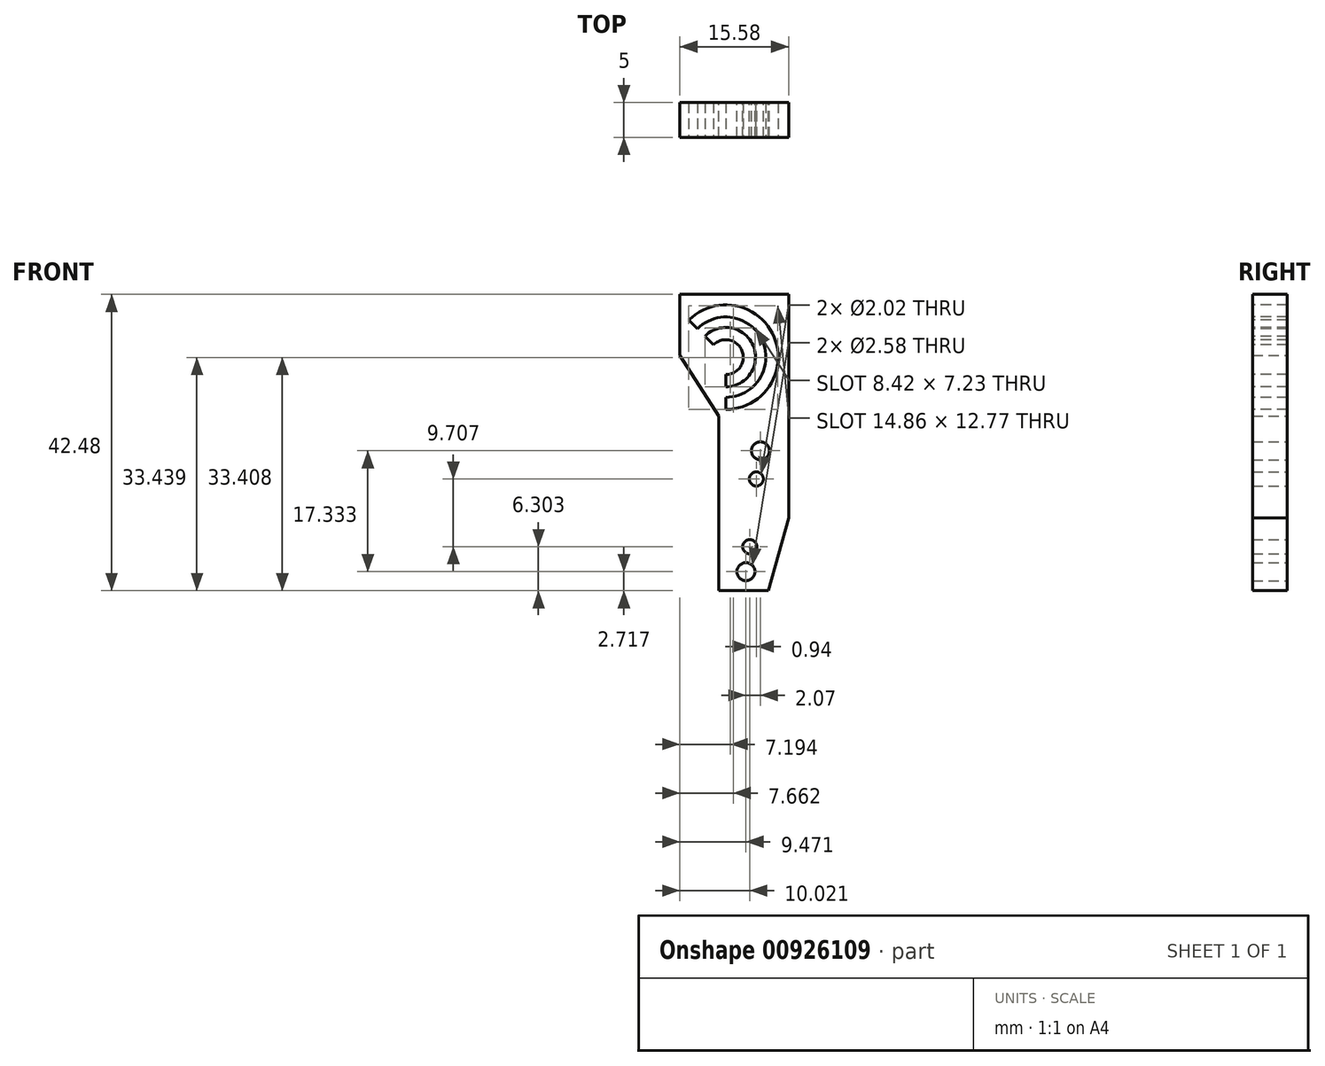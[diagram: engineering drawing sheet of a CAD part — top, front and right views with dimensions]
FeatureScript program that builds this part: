
annotation { "Feature Type Name" : "Feature", "Feature Type Description" : "" }
export const myFeature = defineFeature(function(context is Context, id is Id, definition is map)
    precondition{}
    {
        {
            var Q0;
            Q0=qCreatedBy(makeId("Front.planeOp"),FACE);
            var sketch = newSketch(context, id + "F0", { "sketchPlane" : qUnion([Q0])});
            skLineSegment(sketch, "E0", {"start": v(-37.2, 26.47) * mm, "end": v(-21.63, 26.47) * mm});
            skLineSegment(sketch, "E1", {"start": v(-31.6, -16.01) * mm, "end": v(-24.5, -16.01) * mm});
            skLineSegment(sketch, "E2", {"start": v(-21.63, 26.47) * mm, "end": v(-21.63, -5.57) * mm});
            skLineSegment(sketch, "E3", {"start": v(-21.63, -5.57) * mm, "end": v(-24.5, -16.01) * mm});
            skCircle(sketch, "E4", {"center": v(-27.74, -13.3) * mm, "radius": 1.29 * mm});
            skCircle(sketch, "E5", {"center": v(-27.19, -9.7) * mm, "radius": 1.01 * mm});
            skLineSegment(sketch, "E6", {"start": v(-31.6, 9.02) * mm, "end": v(-31.6, -16.01) * mm});
            skCircle(sketch, "E7", {"center": v(-26.25, 0) * mm, "radius": 1.01 * mm});
            skCircle(sketch, "E8", {"center": v(-25.67, 4.04) * mm, "radius": 1.29 * mm});
            skLineSegment(sketch, "E9", {"start": v(-37.2, 26.47) * mm, "end": v(-37.2, 17.75) * mm});
            skLineSegment(sketch, "E10", {"start": v(-31.6, 9.02) * mm, "end": v(-37.2, 17.75) * mm});
            skSolve(sketch);
        }
        {
            var Q0;
            Q0=qSketchRegion(id+"F0",true);
            extrude(context, id + "F1", {"entities" : qUnion([Q0]), "depth" : 5 * mm, "offsetDistance" : 25 * mm});
        }
        {
            var Q0;
            Q0=makeQuery(id+"F1.opExtrude","CAP_FACE",FACE,{"disambiguationData":[OSD([sQuery(id+"F0.wireOp",EDGE,"E0"),sQuery(id+"F0.wireOp",EDGE,"vhafAufr-sMwy-97n5-iXBO-xDqB0n5jxu3E"),sQuery(id+"F0.wireOp",EDGE,"UXBwDhYX-UGdj-3Fuf-0lg6-L2S2GxCH4KdO"),sQuery(id+"F0.wireOp",EDGE,"E1"),sQuery(id+"F0.wireOp",EDGE,"E2"),sQuery(id+"F0.wireOp",EDGE,"E3"),sQuery(id+"F0.wireOp",EDGE,"E4"),sQuery(id+"F0.wireOp",EDGE,"E5"),sQuery(id+"F0.wireOp",EDGE,"E6"),sQuery(id+"F0.wireOp",EDGE,"E7"),sQuery(id+"F0.wireOp",EDGE,"E8")])],"isStart":false});
            var sketch = newSketch(context, id + "F2", { "sketchPlane" : qUnion([Q0])});
            skArc(sketch, "E11", {"start": v(-30.63, 14.97) * mm, "mid": v(-28.32, 18.43) * mm, "end": v(-32.4, 19.24) * mm});
            skArc(sketch, "E12", {"start": v(-30.63, 13.22) * mm, "mid": v(-26.7, 19.1) * mm, "end": v(-33.63, 20.48) * mm});
            skArc(sketch, "E13", {"start": v(-30.63, 11.72) * mm, "mid": v(-25.32, 19.67) * mm, "end": v(-34.7, 21.54) * mm});
            skArc(sketch, "E14", {"start": v(-30.63, 9.97) * mm, "mid": v(-23.7, 20.34) * mm, "end": v(-35.93, 22.77) * mm});
            skLineSegment(sketch, "E15", {"start": v(-30.63, 14.97) * mm, "end": v(-30.63, 13.22) * mm});
            skLineSegment(sketch, "E16", {"start": v(-32.4, 19.24) * mm, "end": v(-33.63, 20.48) * mm});
            skLineSegment(sketch, "E17.trimOffspring", {"start": v(-34.7, 21.54) * mm, "end": v(-35.93, 22.77) * mm});
            skLineSegment(sketch, "E18.trimOffspring", {"start": v(-30.63, 11.72) * mm, "end": v(-30.63, 9.97) * mm});
            skSolve(sketch);
        }
        {
            var Q0;
            Q0=qSketchRegion(id+"F2",true);
            extrude(context, id + "F3", {"entities" : qUnion([Q0]), "operationType" : NewBodyOperationType.REMOVE, "endBound" : BoundingType.THROUGH_ALL, "oppositeDirection" : true, "depth" : 25 * mm, "offsetDistance" : 25 * mm});
        }
    });
